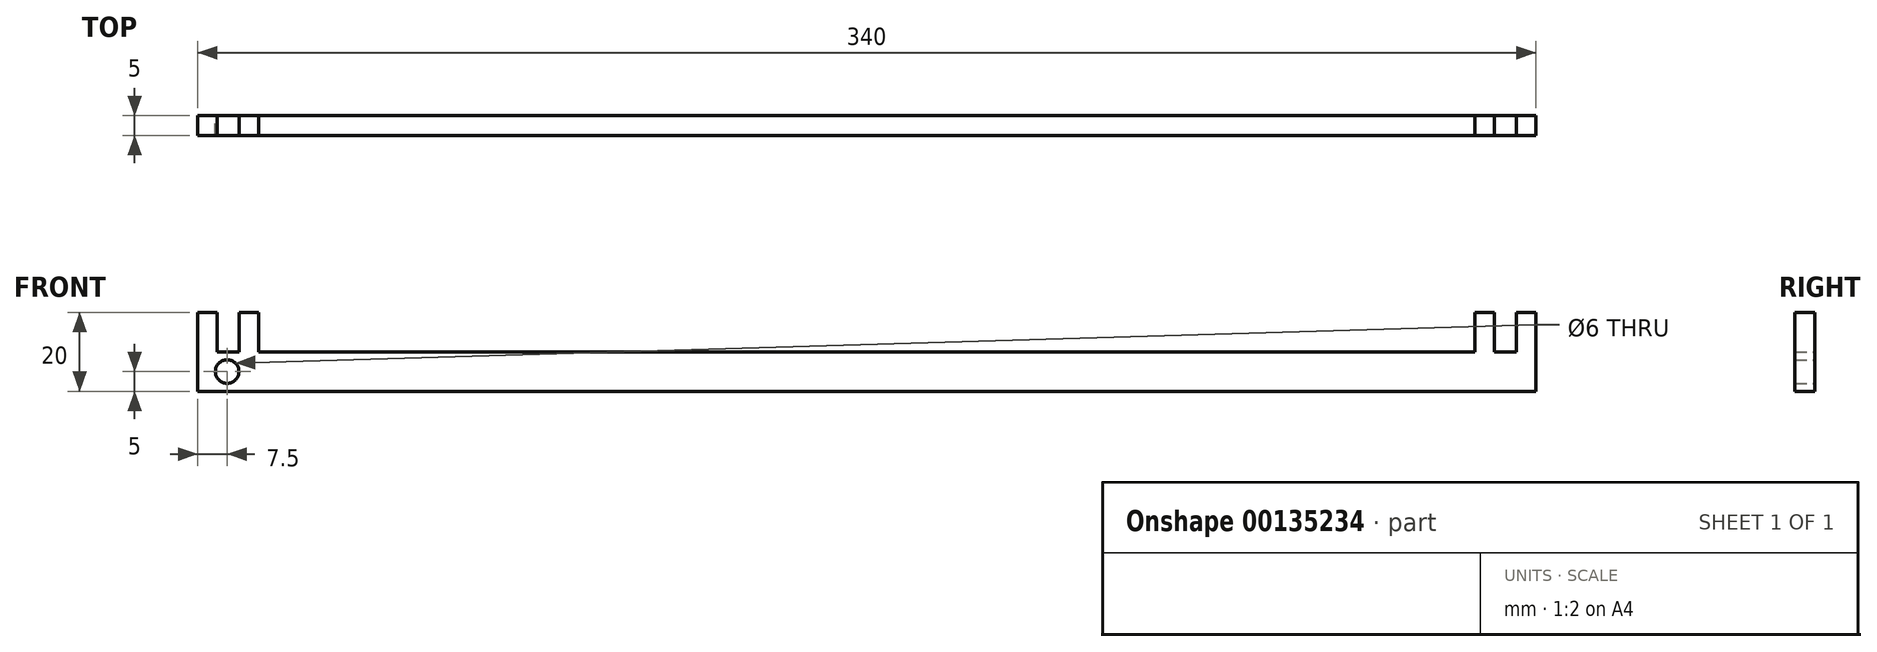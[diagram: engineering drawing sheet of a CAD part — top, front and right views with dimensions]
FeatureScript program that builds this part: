
annotation { "Feature Type Name" : "Feature", "Feature Type Description" : "" }
export const myFeature = defineFeature(function(context is Context, id is Id, definition is map)
    precondition{}
    {
        {
            var Q0;
            Q0=qCreatedBy(makeId("Front.planeOp"),FACE);
            var sketch = newSketch(context, id + "F0", { "sketchPlane" : qUnion([Q0])});
            skLineSegment(sketch, "E0.bottom", {"start": v(170, -10) * mm, "end": v(-170, -10) * mm});
            skLineSegment(sketch, "E0.top", {"start": v(170, 10) * mm, "end": v(165, 10) * mm});
            skLineSegment(sketch, "E0.left", {"start": v(170, -10) * mm, "end": v(170, 10) * mm});
            skLineSegment(sketch, "E0.right", {"start": v(-170, -10) * mm, "end": v(-170, 10) * mm});
            skPoint(sketch, "E0.middle", {"position": v(0, 0) * mm});
            skLineSegment(sketch, "E1", {"start": v(-165, 10) * mm, "end": v(-165, 0) * mm});
            skLineSegment(sketch, "E2", {"start": v(-165, 0) * mm, "end": v(-159.5, 0) * mm});
            skLineSegment(sketch, "E3", {"start": v(165, 0) * mm, "end": v(165, 10) * mm});
            skLineSegment(sketch, "E4.trimOffspring", {"start": v(-165, 10) * mm, "end": v(-170, 10) * mm});
            skLineSegment(sketch, "E5", {"start": v(-159.5, 0) * mm, "end": v(-159.5, 10) * mm});
            skLineSegment(sketch, "E6", {"start": v(-159.5, 10) * mm, "end": v(-154.5, 10) * mm});
            skLineSegment(sketch, "E7", {"start": v(-154.5, 10) * mm, "end": v(-154.5, 0) * mm});
            skLineSegment(sketch, "E8", {"start": v(159.5, 0) * mm, "end": v(159.5, 10) * mm});
            skLineSegment(sketch, "E9", {"start": v(159.5, 10) * mm, "end": v(154.5, 10) * mm});
            skLineSegment(sketch, "E10", {"start": v(154.5, 10) * mm, "end": v(154.5, 0) * mm});
            skLineSegment(sketch, "E11.trimOffspring", {"start": v(159.5, 0) * mm, "end": v(165, 0) * mm});
            skLineSegment(sketch, "E12.trimOffspring", {"start": v(-154.5, 0) * mm, "end": v(154.5, 0) * mm});
            skCircle(sketch, "E13", {"center": v(-162.5, -5) * mm, "radius": 3 * mm});
            skSolve(sketch);
        }
        {
            var Q0;
            Q0=makeQuery(id+"F0.imprint","IMPRINT",FACE,{"disambiguationData":[TD([[makeQuery(id+"F0.imprint","IMPRINT",EDGE,{"derivedFrom":sQuery(id+"F0.wireOp",EDGE,"E0.bottom")}),-1.0]])]});
            extrude(context, id + "F1", {"entities" : qUnion([Q0]), "depth" : 5 * mm});
        }
    });
